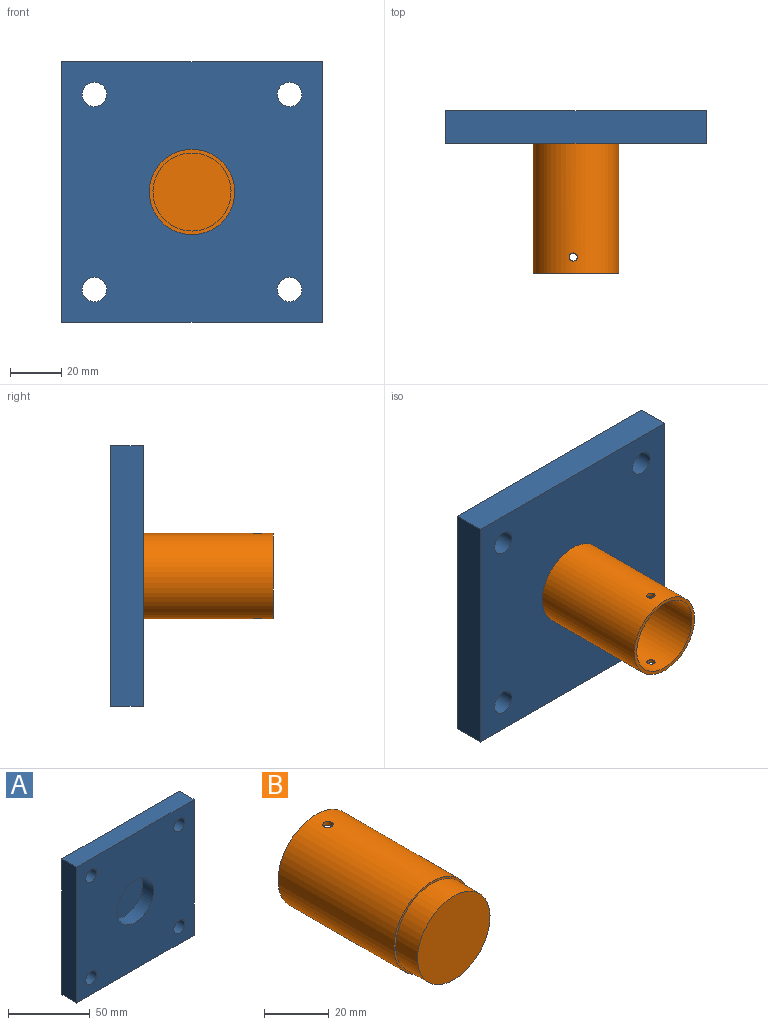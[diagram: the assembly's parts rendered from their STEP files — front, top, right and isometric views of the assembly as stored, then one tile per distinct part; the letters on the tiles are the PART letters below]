
ASSEMBLY  parts=2 mates=1
PART A: 12 faces, bbox 101.6x12.7x101.6 mm
  f0: plane 101.6x12.7mm, normal (0,0,1), area 1290.3mm2, adj f1,f3,f4,f5
  f1: plane 101.6x12.7mm, normal (-1,0,0), area 1290.3mm2, adj f0,f2,f4,f5
  f2: plane 101.6x12.7mm, normal (0,0,-1), area 1290.3mm2, adj f1,f3,f4,f5
  f3: plane 101.6x12.7mm, normal (1,0,0), area 1290.3mm2, adj f0,f2,f4,f5
  f4: plane 101.6x101.6mm, normal (0,-1,0), area 9245.8mm2, adj f0,f1,f2,f3,f6,f8,f9,f10
  f5: plane 101.6x101.6mm, normal (0,1,0), area 10037.5mm2, adj f0,f1,f2,f3,f8,f9,f10,f11
  f6: cylinder r=15.88mm len=31.75mm, axis (0,-1,0), area 950.1mm2, adj f4,f7
  f7: plane 31.75x31.75mm, normal (0,-1,0), area 791.7mm2, adj f6
  f8: cylinder r=4.76mm len=12.7mm, axis (0,-1,0), area 380mm2, adj f4,f5
  f9: cylinder r=4.76mm len=12.7mm, axis (0,-1,0), area 380mm2, adj f4,f5
  f10: cylinder r=4.76mm len=12.7mm, axis (0,-1,0), area 380mm2, adj f4,f5
  f11: cylinder r=4.76mm len=12.7mm, axis (0,-1,0), area 380mm2, adj f4,f5
PART B: 9 faces, bbox 33.3x60.3x33.3 mm
  f0: cylinder r=16.67mm len=50.8mm, axis (0,1,0), area 5304.5mm2, adj f2,f3,f7,f8
  f1: cylinder r=15.24mm len=44.45mm, axis (0,1,0), area 4240.4mm2, adj f3,f6,f7,f8
  f2: plane 33.34x33.34mm, normal (0,-1,0), area 81.2mm2, adj f0,f4
  f3: plane 33.34x33.34mm, normal (0,1,0), area 143.2mm2, adj f0,f1
  f4: cylinder r=15.88mm len=31.75mm, axis (0,1,0), area 950.1mm2, adj f2,f5
  f5: plane 31.75x31.75mm, normal (0,-1,0), area 791.7mm2, adj f4
  f6: plane 30.48x30.48mm, normal (0,1,0), area 729.7mm2, adj f1
  f7: cylinder r=1.59mm len=3.18mm, axis (0,0,-1), area 14.3mm2, adj f0,f1
  f8: cylinder r=1.59mm len=3.18mm, axis (0,0,-1), area 14.3mm2, adj f0,f1
PLACE A t=(-33.51,11.89,-17.06)mm
PLACE B rot(axis=(1,0,0),180deg) t=(-45.48,-51.61,100.99)mm
MATE fastened B.f0 <-> A.f6  axis (0,1,0) through (-106.13,-0.81,60.09)mm
